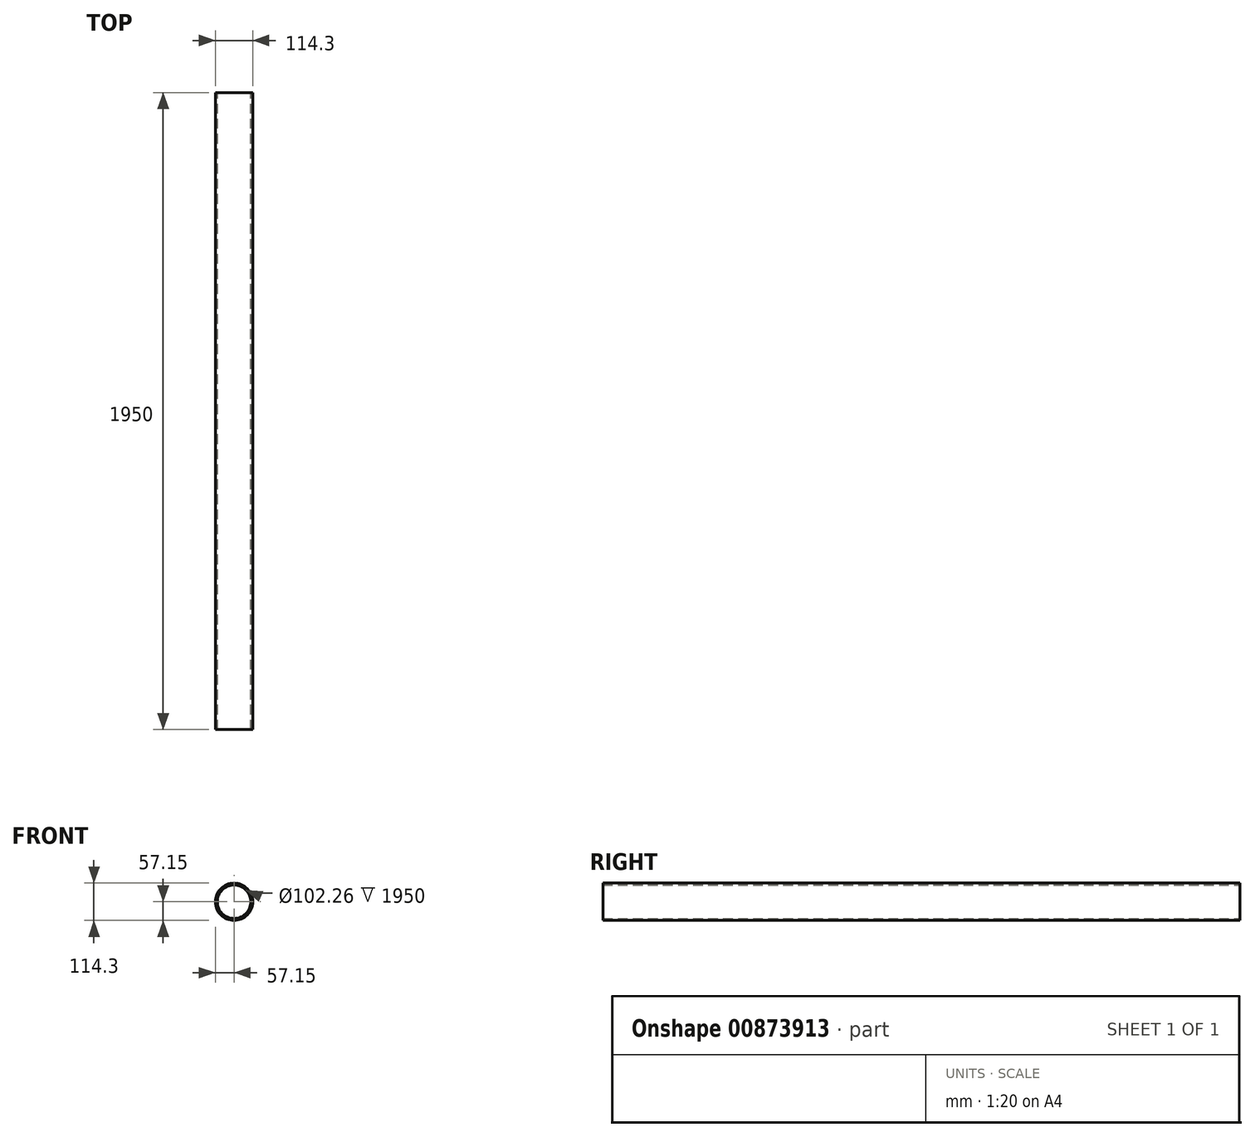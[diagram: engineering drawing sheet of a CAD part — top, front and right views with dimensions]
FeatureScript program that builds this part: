
annotation { "Feature Type Name" : "Feature", "Feature Type Description" : "" }
export const myFeature = defineFeature(function(context is Context, id is Id, definition is map)
    precondition{}
    {
        {
            var Q0;
            Q0=qCreatedBy(makeId("Front.planeOp"),FACE);
            var sketch = newSketch(context, id + "F0", { "sketchPlane" : qUnion([Q0])});
            skCircle(sketch, "E0", {"center": v(0, 0) * mm, "radius": 57.15 * mm});
            skCircle(sketch, "E1", {"center": v(0, 0) * mm, "radius": 51.13 * mm});
            skSolve(sketch);
        }
        {
            var Q0;
            Q0=makeQuery(id+"F0.imprint","IMPRINT",FACE,{"disambiguationData":[TD([[makeQuery(id+"F0.imprint","IMPRINT",EDGE,{"derivedFrom":sQuery(id+"F0.wireOp",EDGE,"E0")}),1.0]])]});
            extrude(context, id + "F1", {"entities" : qUnion([Q0]), "depth" : 1950 * mm, "offsetDistance" : 25 * mm, "symmetric" : true});
        }
    });
